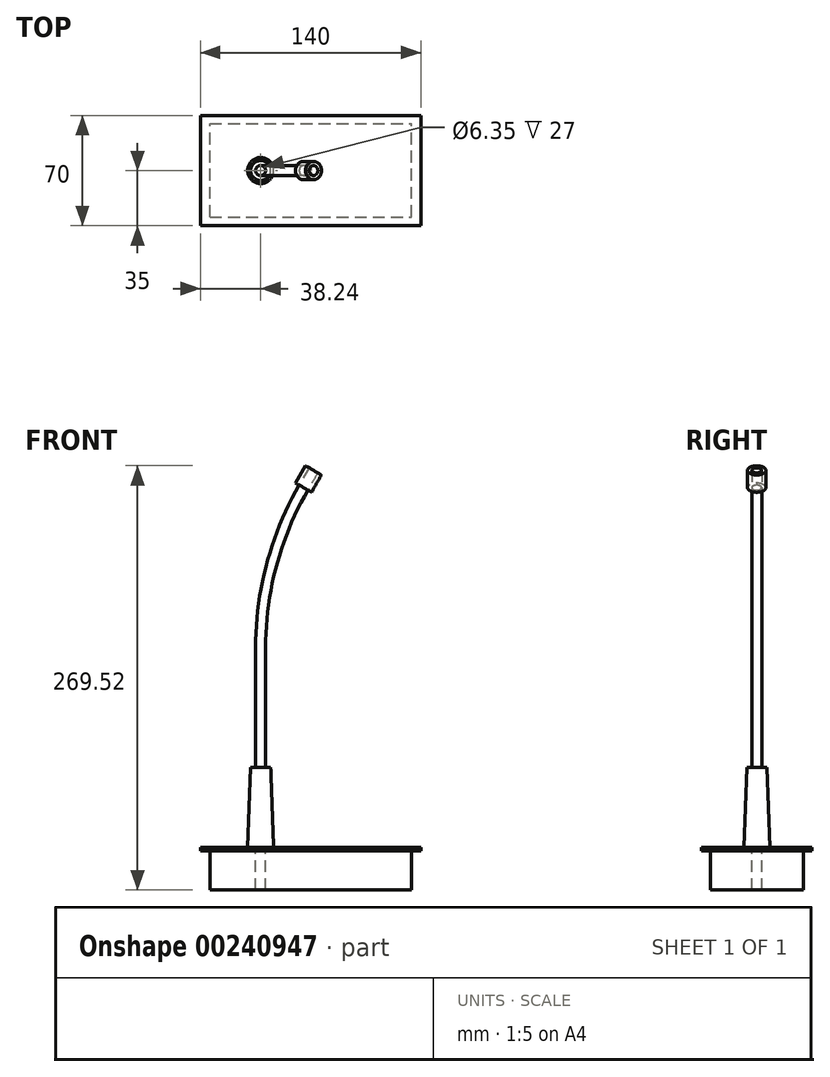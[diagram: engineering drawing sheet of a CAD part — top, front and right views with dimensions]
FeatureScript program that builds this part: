
annotation { "Feature Type Name" : "Feature", "Feature Type Description" : "" }
export const myFeature = defineFeature(function(context is Context, id is Id, definition is map)
    precondition{}
    {
        {
            var Q0;
            Q0=qCreatedBy(makeId("Top.planeOp"),FACE);
            var sketch = newSketch(context, id + "F0", { "sketchPlane" : qUnion([Q0])});
            skCircle(sketch, "E0", {"center": v(0, 0) * mm, "radius": 25.4 * mm});
            skLineSegment(sketch, "E1.bottom", {"start": v(-38.24, -35) * mm, "end": v(101.76, -35) * mm});
            skLineSegment(sketch, "E1.top", {"start": v(-38.24, 35) * mm, "end": v(101.76, 35) * mm});
            skLineSegment(sketch, "E1.left", {"start": v(-38.24, -35) * mm, "end": v(-38.24, 35) * mm});
            skLineSegment(sketch, "E1.right", {"start": v(101.76, -35) * mm, "end": v(101.76, 35) * mm});
            skSolve(sketch);
        }
        {
            var Q0;
            Q0=makeQuery(id+"F0.imprint","IMPRINT",FACE,{"disambiguationData":[TD([[makeQuery(id+"F0.imprint","IMPRINT",EDGE,{"derivedFrom":sQuery(id+"F0.wireOp",EDGE,"E0")}),1.0]])]});
            extrude(context, id + "F1", {"entities" : qUnion([Q0]), "oppositeDirection" : true, "depth" : 19.05 * mm});
        }
        {
            var Q0;
            Q0=makeQuery(id+"F1.opExtrude","CAP_FACE",FACE,{"disambiguationData":[OSD([sQuery(id+"F0.wireOp",EDGE,"E0")])],"isStart":true});
            var sketch = newSketch(context, id + "F2", { "sketchPlane" : qUnion([Q0])});
            skCircle(sketch, "E2", {"center": v(0, 0) * mm, "radius": 8.26 * mm});
            skSolve(sketch);
        }
        {
            var Q0;
            Q0=makeQuery(id+"F2.imprint","IMPRINT",FACE,{"disambiguationData":[TD([[makeQuery(id+"F2.imprint","IMPRINT",EDGE,{"derivedFrom":sQuery(id+"F2.wireOp",EDGE,"E2")}),-1.0]])]});
            cPlane(context, id + "F3", {"entities" : qUnion([Q0]), "cplaneType" : CPlaneType.OFFSET, "offset" : 50.8 * mm, "width" : 152.4 * mm, "height" : 152.4 * mm});
        }
        {
            var Q0;
            Q0=qCreatedBy(id+"F3.planeOp",FACE);
            var sketch = newSketch(context, id + "F4", { "sketchPlane" : qUnion([Q0])});
            skCircle(sketch, "E3", {"center": v(0, 0) * mm, "radius": 6.35 * mm});
            skSolve(sketch);
        }
        {
            var Q1;
            Q1=qSketchRegion(id+"F2",true);
            var Q2;
            Q2=makeQuery(id+"F4.imprint","IMPRINT",FACE,{"disambiguationData":[TD([[makeQuery(id+"F4.imprint","IMPRINT",EDGE,{"derivedFrom":sQuery(id+"F4.wireOp",EDGE,"E3")}),1.0]])]});
            loft(context, id + "F5", {"operationType" : NewBodyOperationType.ADD, "sheetProfilesArray" : [{ "sheetProfileEntities" : qUnion([Q1]) }, { "sheetProfileEntities" : qUnion([Q2]) }]});
        }
        {
            var Q0;
            Q0=qCreatedBy(id+"F3.planeOp",FACE);
            var sketch = newSketch(context, id + "F6", { "sketchPlane" : qUnion([Q0])});
            skCircle(sketch, "E4", {"center": v(0, 0) * mm, "radius": 3.18 * mm});
            skSolve(sketch);
        }
        {
            var Q0;
            Q0=sQuery(id+"F6.wireOp",VERTEX,"E4.center");
            var Q1;
            Q1=makeQuery(id+"F1.opExtrude","SWEPT_BODY",BODY,{"disambiguationData":[OSD([sQuery(id+"F0.wireOp",EDGE,"E0")])]});
            hole(context, id + "F7", {"style" : HoleStyle.SIMPLE, "holeDiameter" : 6.35 * mm, "endStyle" : HoleEndStyle.THROUGH, "locations" : qUnion([Q0]), "scope" : qUnion([Q1])});
        }
        {
            var Q0;
            Q0=qCreatedBy(makeId("Front.planeOp"),FACE);
            var sketch = newSketch(context, id + "F8", { "sketchPlane" : qUnion([Q0])});
            skLineSegment(sketch, "E5", {"start": v(0, 0) * mm, "end": v(0, 127) * mm});
            skArc(sketch, "E6", {"start": v(0, 127) * mm, "mid": v(6.92, 179.6) * mm, "end": v(27.22, 228.6) * mm});
            skLineSegment(sketch, "E7", {"start": v(0, 127) * mm, "end": v(203.2, 127) * mm, "construction": true});
            skLineSegment(sketch, "E8", {"start": v(203.2, 127) * mm, "end": v(27.22, 228.6) * mm, "construction": true});
            skSolve(sketch);
        }
        {
            var Q0;
            Q0=makeQuery(id+"F1.opExtrude","CAP_FACE",FACE,{"disambiguationData":[OSD([sQuery(id+"F0.wireOp",EDGE,"E0")])],"isStart":true});
            var sketch = newSketch(context, id + "F9", { "sketchPlane" : qUnion([Q0])});
            skCircle(sketch, "E9", {"center": v(0, 0) * mm, "radius": 3.18 * mm});
            skSolve(sketch);
        }
        {
            var Q0;
            Q0=qSketchRegion(id+"F9",true);
            var Q1;
            Q1=qBodyType(qCreatedBy(id+"F8",EDGE),BodyType.WIRE);
            sweep(context, id + "F10", {"operationType" : NewBodyOperationType.ADD, "profiles" : qUnion([Q0]), "path" : qUnion([Q1])});
        }
        {
            var Q0;
            Q0=makeQuery(id+"F10.opSweep","CAP_FACE",FACE,{"disambiguationData":[OSD([sQuery(id+"F8.wireOp",VERTEX,"E6.end"),sQuery(id+"F9.wireOp",EDGE,"E9")])],"isStart":false});
            var sketch = newSketch(context, id + "F11", { "sketchPlane" : qUnion([Q0])});
            skCircle(sketch, "E10", {"center": v(-90.72, 0) * mm, "radius": 5.84 * mm});
            skSolve(sketch);
        }
        {
            var Q0;
            Q0=makeQuery(id+"F11.imprint","IMPRINT",FACE,{"disambiguationData":[TD([[makeQuery(id+"F11.imprint","IMPRINT",EDGE,{"derivedFrom":sQuery(id+"F11.wireOp",EDGE,"E10")}),1.0]])]});
            extrude(context, id + "F12", {"entities" : qUnion([Q0]), "depth" : 12.7 * mm});
        }
        {
            var Q0;
            Q0=makeQuery(id+"F12.opExtrude","CAP_FACE",FACE,{"disambiguationData":[OSD([sQuery(id+"F8.wireOp",VERTEX,"E6.end"),sQuery(id+"F9.wireOp",EDGE,"E9"),sQuery(id+"F11.wireOp",EDGE,"E10")])],"isStart":false});
            var sketch = newSketch(context, id + "F13", { "sketchPlane" : qUnion([Q0])});
            skPoint(sketch, "E11", {"position": v(-90.72, 0) * mm});
            skSolve(sketch);
        }
        {
            var Q0;
            Q0=sQuery(id+"F13.wireOp",VERTEX,"E11");
            var Q1;
            Q1=qCreatedBy(makeId("Front.planeOp"),FACE);
            cPlane(context, id + "F14", {"entities" : qUnion([Q0, Q1]), "cplaneType" : CPlaneType.PLANE_POINT, "offset" : 152.4 * mm, "width" : 152.4 * mm, "height" : 152.4 * mm});
        }
        {
            var Q0;
            Q0 = qSketchRegion(id + "F0", true);
            extrude(context, id + "F15", {"entities" : qUnion([Q0]), "operationType" : NewBodyOperationType.ADD, "oppositeDirection" : true, "depth" : 2 * mm});
        }
        {
            var Q0;
            Q0=makeQuery(id+"F15.opExtrude","CAP_FACE",FACE,{"disambiguationData":[OSD([sQuery(id+"F0.wireOp",EDGE,"E0"),sQuery(id+"F0.wireOp",EDGE,"E1.bottom"),sQuery(id+"F0.wireOp",EDGE,"E1.top"),sQuery(id+"F0.wireOp",EDGE,"E1.left"),sQuery(id+"F0.wireOp",EDGE,"E1.right")])],"isStart":false});
            var sketch = newSketch(context, id + "F16", { "sketchPlane" : qUnion([Q0])});
            skLineSegment(sketch, "E12.bottom", {"start": v(-32.18, 29.4) * mm, "end": v(95.8, 29.4) * mm});
            skLineSegment(sketch, "E12.top", {"start": v(-32.18, -29.76) * mm, "end": v(95.8, -29.76) * mm});
            skLineSegment(sketch, "E12.left", {"start": v(-32.18, 29.4) * mm, "end": v(-32.18, -29.76) * mm});
            skLineSegment(sketch, "E12.right", {"start": v(95.8, 29.4) * mm, "end": v(95.8, -29.76) * mm});
            skSolve(sketch);
        }
        {
            var Q0;
            Q0=makeQuery(id+"F16.imprint","IMPRINT",FACE,{"disambiguationData":[TD([[makeQuery(id+"F16.imprint","IMPRINT",EDGE,{"derivedFrom":sQuery(id+"F16.wireOp",EDGE,"E12.bottom")}),-1.0]])]});
            extrude(context, id + "F17", {"entities" : qUnion([Q0]), "operationType" : NewBodyOperationType.ADD, "depth" : 25 * mm});
        }
        {
            var Q0;
            Q0=makeQuery(id+"F1.opExtrude","CAP_FACE",FACE,{"disambiguationData":[OSD([sQuery(id+"F0.wireOp",EDGE,"E0")])],"isStart":false});
            var Q1;
            Q1=makeQuery(id+"F17.opExtrude","CAP_FACE",FACE,{"disambiguationData":[OSD([sQuery(id+"F0.wireOp",EDGE,"E0"),sQuery(id+"F16.wireOp",EDGE,"E12.bottom"),sQuery(id+"F16.wireOp",EDGE,"E12.top"),sQuery(id+"F16.wireOp",EDGE,"E12.left"),sQuery(id+"F16.wireOp",EDGE,"E12.right")])],"isStart":false});
            extrude(context, id + "F18", {"entities" : qUnion([Q0]), "operationType" : NewBodyOperationType.ADD, "endBound" : BoundingType.UP_TO_SURFACE, "endBoundEntityFace" : qUnion([Q1]), "depth" : 25 * mm});
        }
    });
